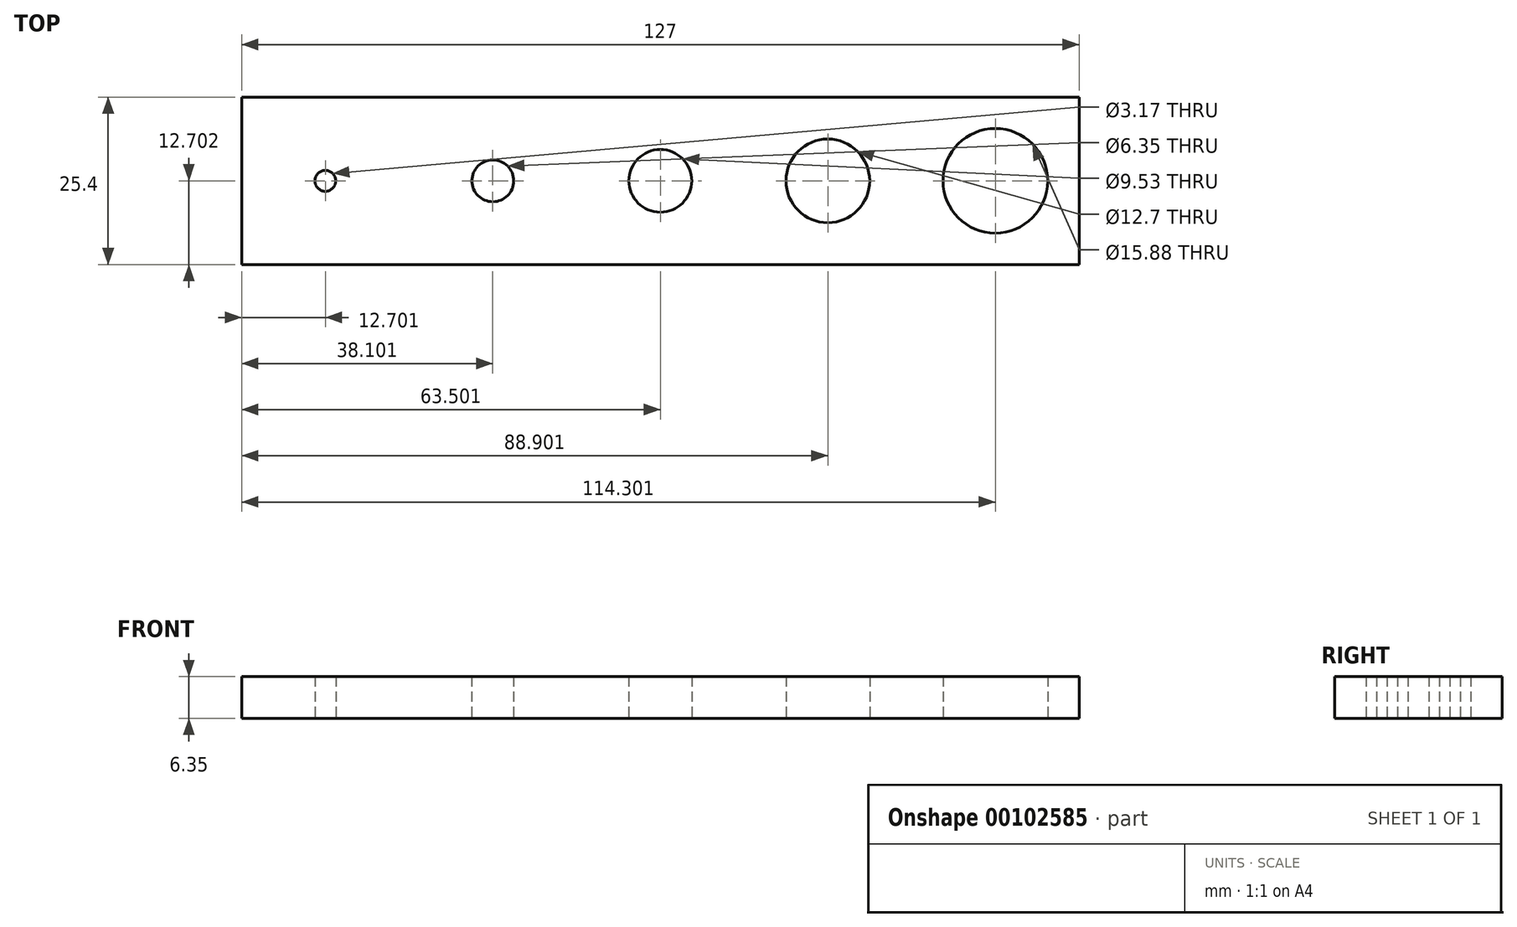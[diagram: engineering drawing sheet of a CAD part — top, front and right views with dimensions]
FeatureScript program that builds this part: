
annotation { "Feature Type Name" : "Feature", "Feature Type Description" : "" }
export const myFeature = defineFeature(function(context is Context, id is Id, definition is map)
    precondition{}
    {
        {
            var Q0;
            Q0=qCreatedBy(makeId("Top.planeOp"),FACE);
            var sketch = newSketch(context, id + "F0", { "sketchPlane" : qUnion([Q0])});
            skLineSegment(sketch, "E0.bottom", {"start": v(-63.02, -7.17) * mm, "end": v(63.98, -7.17) * mm});
            skLineSegment(sketch, "E0.top", {"start": v(-63.02, -32.57) * mm, "end": v(63.98, -32.57) * mm});
            skLineSegment(sketch, "E0.left", {"start": v(-63.02, -7.17) * mm, "end": v(-63.02, -32.57) * mm});
            skLineSegment(sketch, "E0.right", {"start": v(63.98, -7.17) * mm, "end": v(63.98, -32.57) * mm});
            skCircle(sketch, "E1", {"center": v(-50.32, -19.87) * mm, "radius": 1.59 * mm});
            skCircle(sketch, "E2", {"center": v(-24.92, -19.87) * mm, "radius": 3.18 * mm});
            skCircle(sketch, "E3", {"center": v(0.48, -19.87) * mm, "radius": 4.76 * mm});
            skCircle(sketch, "E4", {"center": v(25.88, -19.87) * mm, "radius": 6.35 * mm});
            skCircle(sketch, "E5", {"center": v(51.28, -19.87) * mm, "radius": 7.94 * mm});
            skSolve(sketch);
        }
        {
            var Q0;
            Q0=makeQuery(id+"F0.imprint","IMPRINT",FACE,{"disambiguationData":[TD([[makeQuery(id+"F0.imprint","IMPRINT",EDGE,{"derivedFrom":sQuery(id+"F0.wireOp",EDGE,"E0.bottom")}),-1.0]])]});
            extrude(context, id + "F1", {"entities" : qUnion([Q0]), "depth" : 6.35 * mm});
        }
    });
